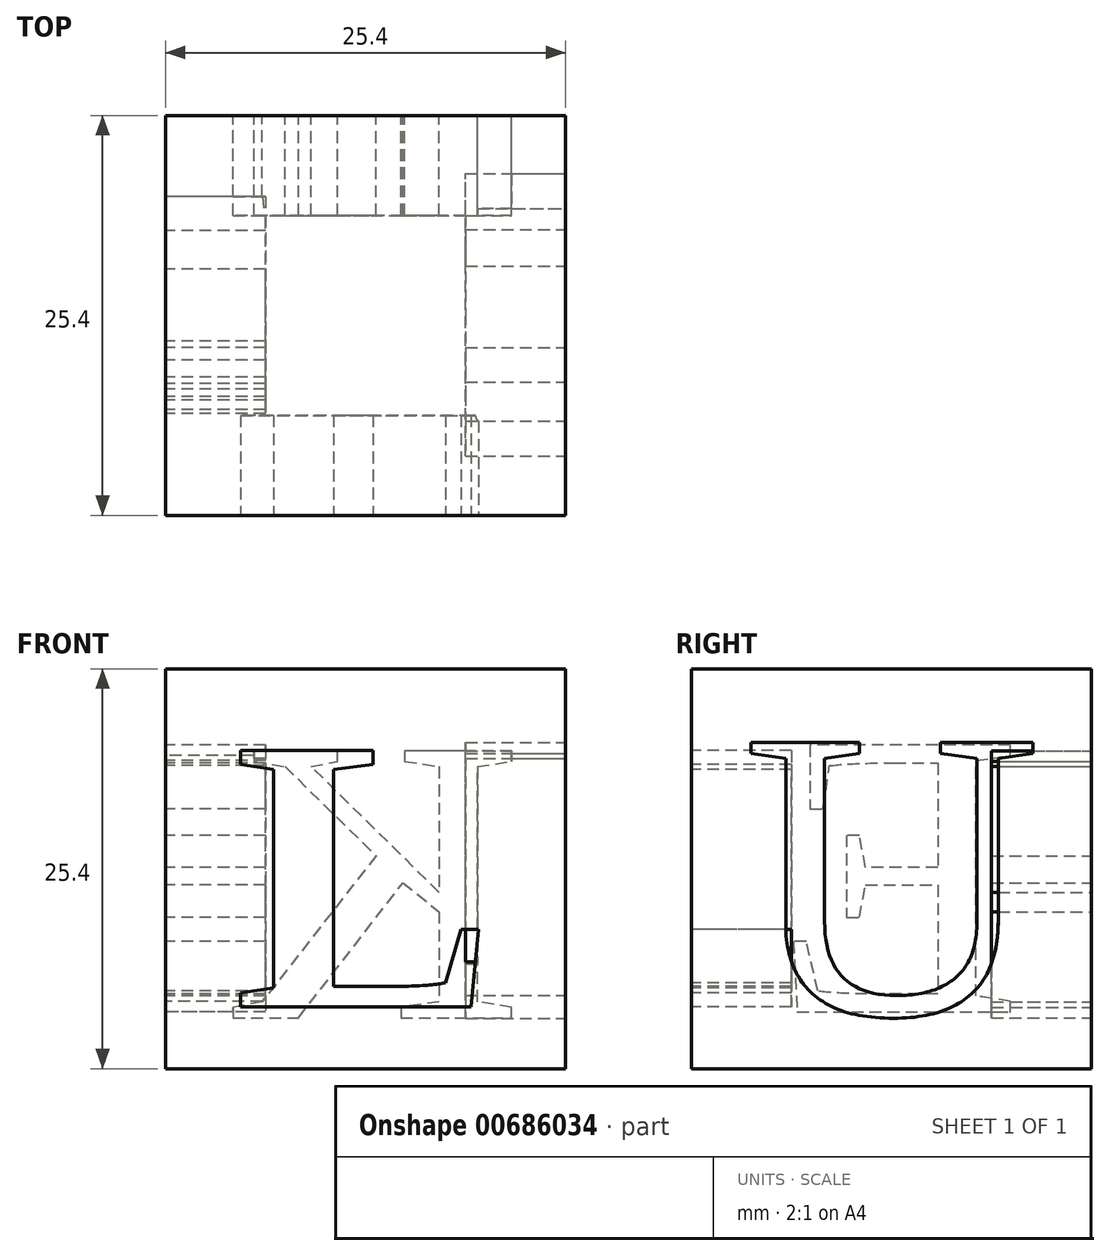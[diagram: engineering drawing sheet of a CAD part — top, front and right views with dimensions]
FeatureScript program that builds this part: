
annotation { "Feature Type Name" : "Feature", "Feature Type Description" : "" }
export const myFeature = defineFeature(function(context is Context, id is Id, definition is map)
    precondition{}
    {
        {
            var Q0;
            Q0=qCreatedBy(makeId("Front.planeOp"),FACE);
            var sketch = newSketch(context, id + "F0", { "sketchPlane" : qUnion([Q0])});
            skLineSegment(sketch, "E0.bottom", {"start": v(-12.7, 12.7) * mm, "end": v(12.7, 12.7) * mm});
            skLineSegment(sketch, "E0.top", {"start": v(-12.7, -12.7) * mm, "end": v(12.7, -12.7) * mm});
            skLineSegment(sketch, "E0.left", {"start": v(-12.7, 12.7) * mm, "end": v(-12.7, -12.7) * mm});
            skLineSegment(sketch, "E0.right", {"start": v(12.7, 12.7) * mm, "end": v(12.7, -12.7) * mm});
            skPoint(sketch, "E0.middle", {"position": v(0, 0) * mm});
            skSolve(sketch);
        }
        {
            var Q0;
            Q0 = qSketchRegion(id + "F0", true);
            extrude(context, id + "F1", {"entities" : qUnion([Q0]), "depth" : 25.4 * mm, "offsetDistance" : 25.4 * mm});
        }
        {
            var Q0;
            Q0=makeQuery(id+"F1.opExtrude","CAP_FACE",FACE,{"disambiguationData":[OSD([sQuery(id+"F0.wireOp",EDGE,"E0.bottom"),sQuery(id+"F0.wireOp",EDGE,"E0.top"),sQuery(id+"F0.wireOp",EDGE,"E0.left"),sQuery(id+"F0.wireOp",EDGE,"E0.right")])],"isStart":false});
            var sketch = newSketch(context, id + "F2", { "sketchPlane" : qUnion([Q0])});
            skText(sketch, "E1", { "text": "L", "fontName": "Tinos-Bold.ttf"});
            const initialGuessF2  = {"E1": [-0.00836, -0.00877, 1, 0, 0.01789]};
            skSetInitialGuess(sketch, initialGuessF2);
            skSolve(sketch);
        }
        {
            var Q0;
            Q0=makeQuery(id+"F1.opExtrude","SWEPT_FACE",FACE,{"disambiguationData":[OSD([sQuery(id+"F0.wireOp",EDGE,"E0.right")])]});
            var sketch = newSketch(context, id + "F3", { "sketchPlane" : qUnion([Q0])});
            skText(sketch, "E2", { "text": "U", "fontName": "Tinos-Regular.ttf"});
            const initialGuessF3  = {"E2": [-0.02218, -0.00924, 1, 0, 0.01897]};
            skSetInitialGuess(sketch, initialGuessF3);
            skSolve(sketch);
        }
        {
            var Q0;
            Q0=makeQuery(id+"F1.opExtrude","SWEPT_FACE",FACE,{"disambiguationData":[OSD([sQuery(id+"F0.wireOp",EDGE,"E0.left")])]});
            var sketch = newSketch(context, id + "F4", { "sketchPlane" : qUnion([Q0])});
            skText(sketch, "E3", { "text": "E", "fontName": "Tinos-Regular.ttf"});
            const initialGuessF4  = {"E3": [0.0044, -0.0091, 1, 0, 0.01865]};
            skSetInitialGuess(sketch, initialGuessF4);
            skSolve(sketch);
        }
        {
            var Q0;
            Q0 = qSketchRegion(id + "F2", true);
            extrude(context, id + "F5", {"entities" : qUnion([Q0]), "operationType" : NewBodyOperationType.REMOVE, "oppositeDirection" : true, "depth" : 6.35 * mm, "offsetDistance" : 25.4 * mm});
        }
        {
            var Q0;
            Q0 = qSketchRegion(id + "F4", true);
            extrude(context, id + "F6", {"entities" : qUnion([Q0]), "operationType" : NewBodyOperationType.REMOVE, "oppositeDirection" : true, "depth" : 6.35 * mm, "offsetDistance" : 25.4 * mm});
        }
        {
            var Q0;
            Q0 = qSketchRegion(id + "F3", true);
            extrude(context, id + "F7", {"entities" : qUnion([Q0]), "operationType" : NewBodyOperationType.REMOVE, "oppositeDirection" : true, "depth" : 6.35 * mm, "offsetDistance" : 25.4 * mm});
        }
        {
            var Q0;
            Q0=makeQuery(id+"F1.opExtrude","CAP_FACE",FACE,{"disambiguationData":[OSD([sQuery(id+"F0.wireOp",EDGE,"E0.bottom"),sQuery(id+"F0.wireOp",EDGE,"E0.top"),sQuery(id+"F0.wireOp",EDGE,"E0.left"),sQuery(id+"F0.wireOp",EDGE,"E0.right")])],"isStart":true});
            var sketch = newSketch(context, id + "F8", { "sketchPlane" : qUnion([Q0])});
            skText(sketch, "E4", { "text": "K", "fontName": "Tinos-Regular.ttf"});
            const initialGuessF8  = {"E4": [-0.01003, -0.00947, 1, 0, 0.01865]};
            skSetInitialGuess(sketch, initialGuessF8);
            skSolve(sketch);
        }
        {
            var Q0;
            Q0 = qSketchRegion(id + "F8", true);
            extrude(context, id + "F9", {"entities" : qUnion([Q0]), "operationType" : NewBodyOperationType.REMOVE, "oppositeDirection" : true, "depth" : 6.35 * mm, "offsetDistance" : 25.4 * mm});
        }
    });
